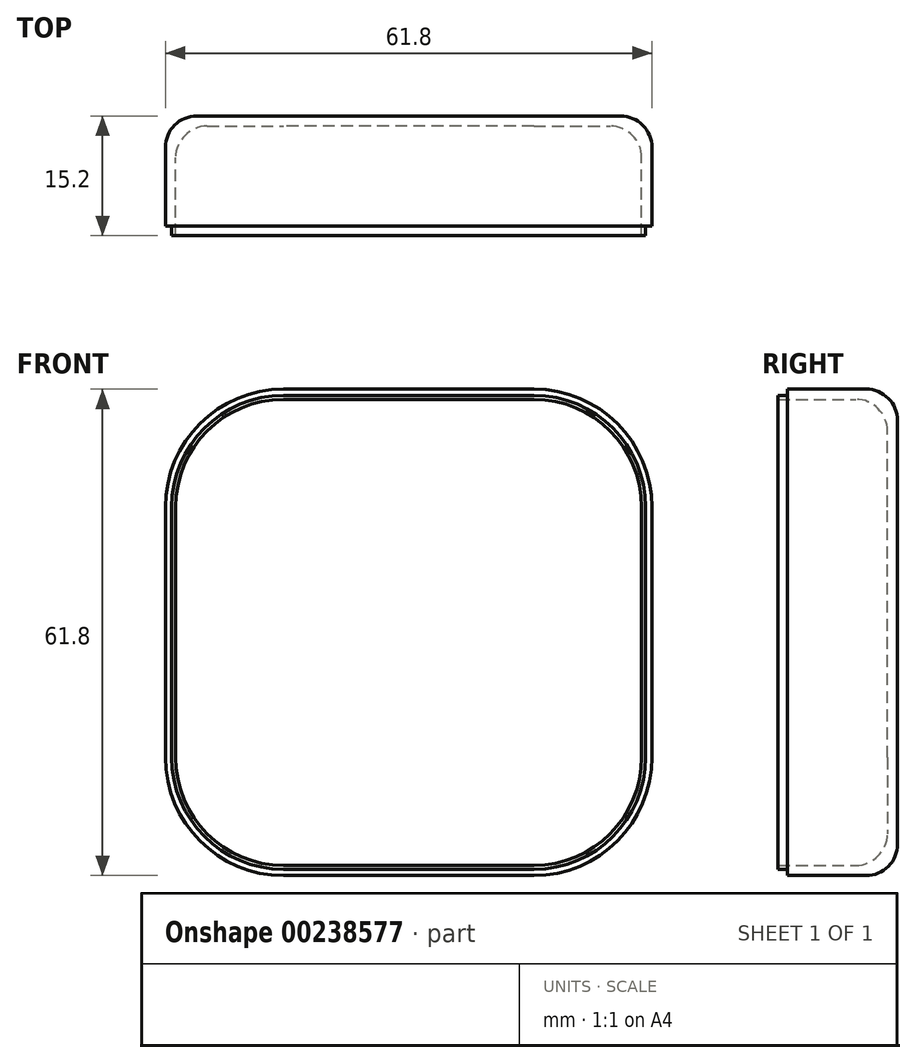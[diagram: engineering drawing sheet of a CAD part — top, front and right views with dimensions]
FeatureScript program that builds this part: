
annotation { "Feature Type Name" : "Feature", "Feature Type Description" : "" }
export const myFeature = defineFeature(function(context is Context, id is Id, definition is map)
    precondition{}
    {
        {
            var Q0;
            Q0=qCreatedBy(makeId("Front.planeOp"),FACE);
            var sketch = newSketch(context, id + "F0", { "sketchPlane" : qUnion([Q0])});
            skLineSegment(sketch, "E0.bottom", {"start": v(-15.9, 30.9) * mm, "end": v(15.9, 30.9) * mm});
            skLineSegment(sketch, "E0.top", {"start": v(-15.9, -30.9) * mm, "end": v(15.9, -30.9) * mm});
            skLineSegment(sketch, "E0.left", {"start": v(-30.9, 15.9) * mm, "end": v(-30.9, -15.9) * mm});
            skLineSegment(sketch, "E0.right", {"start": v(30.9, 15.9) * mm, "end": v(30.9, -15.9) * mm});
            skPoint(sketch, "E0.middle", {"position": v(0, 0) * mm});
            skPoint(sketch, "E1.visualSharp", {"position": v(-30.9, 30.9) * mm});
            skArc(sketch, "E1.filletArc", {"start": v(-15.9, 30.9) * mm, "mid": v(-26.5, 26.5) * mm, "end": v(-30.9, 15.9) * mm});
            skPoint(sketch, "E2.visualSharp", {"position": v(30.9, 30.9) * mm});
            skArc(sketch, "E2.filletArc", {"start": v(30.9, 15.9) * mm, "mid": v(26.5, 26.5) * mm, "end": v(15.9, 30.9) * mm});
            skPoint(sketch, "E3.visualSharp", {"position": v(30.9, -30.9) * mm});
            skArc(sketch, "E3.filletArc", {"start": v(15.9, -30.9) * mm, "mid": v(26.5, -26.5) * mm, "end": v(30.9, -15.9) * mm});
            skPoint(sketch, "E4.visualSharp", {"position": v(-30.9, -30.9) * mm});
            skArc(sketch, "E4.filletArc", {"start": v(-30.9, -15.9) * mm, "mid": v(-26.5, -26.5) * mm, "end": v(-15.9, -30.9) * mm});
            skLineSegment(sketch, "E5.0", {"start": v(-15.9, 29.6) * mm, "end": v(15.9, 29.6) * mm});
            skArc(sketch, "E5.1", {"start": v(29.6, 15.9) * mm, "mid": v(25.59, 25.59) * mm, "end": v(15.9, 29.6) * mm});
            skArc(sketch, "E5.2", {"start": v(-15.9, 29.6) * mm, "mid": v(-25.59, 25.59) * mm, "end": v(-29.6, 15.9) * mm});
            skLineSegment(sketch, "E5.3", {"start": v(29.6, 15.9) * mm, "end": v(29.6, -15.9) * mm});
            skLineSegment(sketch, "E5.4", {"start": v(-29.6, 15.9) * mm, "end": v(-29.6, -15.9) * mm});
            skArc(sketch, "E5.5", {"start": v(-29.6, -15.9) * mm, "mid": v(-25.59, -25.59) * mm, "end": v(-15.9, -29.6) * mm});
            skLineSegment(sketch, "E5.6", {"start": v(-15.9, -29.6) * mm, "end": v(15.9, -29.6) * mm});
            skArc(sketch, "E5.7", {"start": v(15.9, -29.6) * mm, "mid": v(25.59, -25.59) * mm, "end": v(29.6, -15.9) * mm});
            skSolve(sketch);
        }
        {
            var Q0;
            Q0 = qSketchRegion(id + "F0", true);
            var Q1;
            Q1=makeQuery(id+"F0.imprint","IMPRINT",FACE,{"disambiguationData":[TD([[makeQuery(id+"F0.imprint","IMPRINT",EDGE,{"derivedFrom":sQuery(id+"F0.wireOp",EDGE,"E5.0")}),-1.0]])]});
            extrude(context, id + "F1", {"entities" : qUnion([Q0, Q1]), "depth" : 1.3 * mm});
        }
        {
            var Q0;
            Q0 = qSketchRegion(id + "F0", true);
            extrude(context, id + "F2", {"entities" : qUnion([Q0]), "operationType" : NewBodyOperationType.ADD, "depth" : 14 * mm});
        }
        {
            var Q0;
            Q0=makeQuery(id+"F2.opExtrude","CAP_FACE",FACE,{"disambiguationData":[OSD([sQuery(id+"F0.wireOp",EDGE,"E0.bottom"),sQuery(id+"F0.wireOp",EDGE,"E0.top"),sQuery(id+"F0.wireOp",EDGE,"E0.left"),sQuery(id+"F0.wireOp",EDGE,"E0.right"),sQuery(id+"F0.wireOp",EDGE,"E1.filletArc"),sQuery(id+"F0.wireOp",EDGE,"E2.filletArc"),sQuery(id+"F0.wireOp",EDGE,"E3.filletArc"),sQuery(id+"F0.wireOp",EDGE,"E4.filletArc"),sQuery(id+"F0.wireOp",EDGE,"E5.0"),sQuery(id+"F0.wireOp",EDGE,"E5.1"),sQuery(id+"F0.wireOp",EDGE,"E5.2"),sQuery(id+"F0.wireOp",EDGE,"E5.3"),sQuery(id+"F0.wireOp",EDGE,"E5.4"),sQuery(id+"F0.wireOp",EDGE,"E5.5"),sQuery(id+"F0.wireOp",EDGE,"E5.6"),sQuery(id+"F0.wireOp",EDGE,"E5.7")])],"isStart":false});
            var sketch = newSketch(context, id + "F3", { "sketchPlane" : qUnion([Q0])});
            skLineSegment(sketch, "E6.0", {"start": v(-15.9, 30.1) * mm, "end": v(15.9, 30.1) * mm});
            skArc(sketch, "E6.1", {"start": v(30.1, 15.9) * mm, "mid": v(25.94, 25.94) * mm, "end": v(15.9, 30.1) * mm});
            skArc(sketch, "E6.2", {"start": v(-15.9, 30.1) * mm, "mid": v(-25.94, 25.94) * mm, "end": v(-30.1, 15.9) * mm});
            skLineSegment(sketch, "E6.3", {"start": v(30.1, 15.9) * mm, "end": v(30.1, -15.9) * mm});
            skLineSegment(sketch, "E6.4", {"start": v(-30.1, 15.9) * mm, "end": v(-30.1, -15.9) * mm});
            skArc(sketch, "E6.5", {"start": v(-30.1, -15.9) * mm, "mid": v(-25.94, -25.94) * mm, "end": v(-15.9, -30.1) * mm});
            skLineSegment(sketch, "E6.6", {"start": v(-15.9, -30.1) * mm, "end": v(15.9, -30.1) * mm});
            skArc(sketch, "E6.7", {"start": v(15.9, -30.1) * mm, "mid": v(25.94, -25.94) * mm, "end": v(30.1, -15.9) * mm});
            skSolve(sketch);
        }
        {
            var Q0;
            Q0=makeQuery(id+"F3.imprint","IMPRINT",FACE,{"disambiguationData":[TD([[makeQuery(id+"F3.imprint","IMPRINT",EDGE,{"derivedFrom":sQuery(id+"F3.wireOp",EDGE,"E6.0")}),-1.0]])]});
            extrude(context, id + "F4", {"entities" : qUnion([Q0]), "operationType" : NewBodyOperationType.ADD, "depth" : 1.2 * mm});
        }
        {
            var Q0;
            Q0=makeQuery(id+"F2.boolean.opBoolean","INTERSECT",EDGE,{"derivedFrom":[makeQuery(id+"F1.opExtrude","CAP_FACE",FACE,{"disambiguationData":[OSD([sQuery(id+"F0.wireOp",EDGE,"E0.bottom"),sQuery(id+"F0.wireOp",EDGE,"E0.top"),sQuery(id+"F0.wireOp",EDGE,"E0.left"),sQuery(id+"F0.wireOp",EDGE,"E0.right"),sQuery(id+"F0.wireOp",EDGE,"E1.filletArc"),sQuery(id+"F0.wireOp",EDGE,"E2.filletArc"),sQuery(id+"F0.wireOp",EDGE,"E3.filletArc"),sQuery(id+"F0.wireOp",EDGE,"E4.filletArc")])],"isStart":false}),makeQuery(id+"F2.opExtrude","SWEPT_FACE",FACE,{"disambiguationData":[OSD([sQuery(id+"F0.wireOp",EDGE,"E5.5")])]})]});
            fillet(context, id + "F5", {"entities" : qUnion([Q0]), "radius" : 4 * mm, "tangentPropagation" : true, "allowEdgeOverflow" : false});
        }
        {
            var Q0;
            Q0=makeQuery(id+"F1.opExtrude","CAP_FACE",FACE,{"disambiguationData":[OSD([sQuery(id+"F0.wireOp",EDGE,"E0.bottom"),sQuery(id+"F0.wireOp",EDGE,"E0.top"),sQuery(id+"F0.wireOp",EDGE,"E0.left"),sQuery(id+"F0.wireOp",EDGE,"E0.right"),sQuery(id+"F0.wireOp",EDGE,"E1.filletArc"),sQuery(id+"F0.wireOp",EDGE,"E2.filletArc"),sQuery(id+"F0.wireOp",EDGE,"E3.filletArc"),sQuery(id+"F0.wireOp",EDGE,"E4.filletArc")])],"isStart":true});
            fillet(context, id + "F6", {"entities" : qUnion([Q0]), "radius" : 4 * mm, "tangentPropagation" : true, "allowEdgeOverflow" : false});
        }
    });
